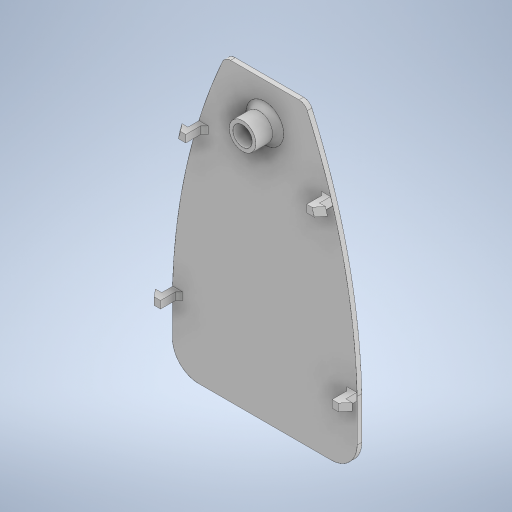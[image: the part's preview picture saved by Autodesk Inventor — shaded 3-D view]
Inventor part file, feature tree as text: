
AUTODESK INVENTOR PART (.ipt)
format: ipt  version: 2023 (Build 270158000, 158)  size: 384,512 bytes
history: native  units: in
note: dims shown in document units (in); Inventor stores cm internally (conversion verified against a paired STEP export)
features: sketch x7, extrude x4, loft x2, fillet x1, plane x1, mirror x1, chamfer x1, projected_geometry x1
ambient origin geometry x8: Origin, YZ Plane, XZ Plane, XY Plane, X Axis, Y Axis, Z Axis, Center Point
bodies: Solid1 (feature_tree)
feature tree (18):
  sketch  "Sketch1"  dims[d0=0.0197in d1=0.0492in d2=0.0in]
  extrude  "Extrusion1"  Depth=0.0492in TaperAngle=0.0deg
  extrude  "Extrusion2"  Depth=0.3937in
  fillet  "Fillet1"  Radius=0.0394in
  extrude  "Extrusion3"  Depth=0.0591in
  loft  "Loft1"
  plane  "Work Plane1"
  loft  "Loft2"
  mirror  "Mirror1"
  chamfer  "Chamfer1"  Distance=0.1969in
  extrude  "Extrusion4"  Depth=0.0787in
  sketch  "Sketch2"  dims[d3=0.2047in d4=0.3937in d5=0.0394in]
  sketch  "Sketch3"  dims[d6=0.2362in d7=0.0in d8=0.0591in]
  projected_geometry  "Projected Loop1"
  sketch  "Sketch4"  dims[d9=0.7272in d10=0.0787in]
  sketch  "Sketch5"  dims[d11=0.0787in d13=0.0787in d14=0.1969in d15=0.0in]
  sketch  "Sketch6"  dims[d16=0.0787in d17=0.0669in]
  sketch  "Sketch7"  dims[d18=0.0787in d19=0.0669in d20=0.0in d21=90.0deg d22=0.0in d23=90.0deg d24=0.0787in d25=0.063in d26=0.0787in d27=0.063in d28=0.0in d29=90.0deg d30=0.0in d31=90.0deg d32=0.0394in d33=0.125in d34=45.0deg d35=0.0492in d36=0.0in]
